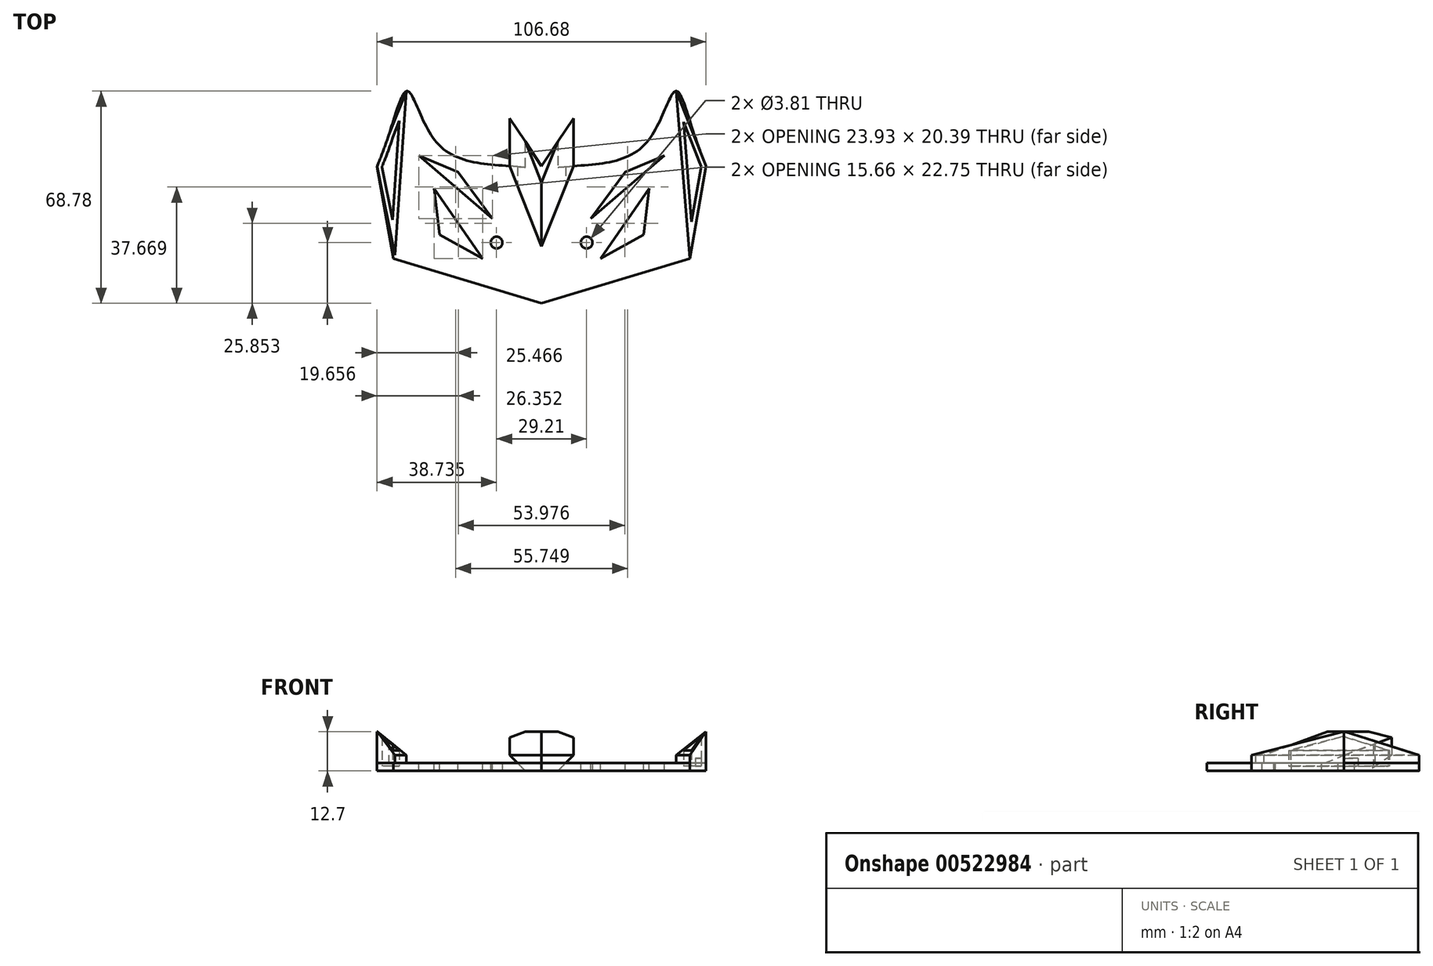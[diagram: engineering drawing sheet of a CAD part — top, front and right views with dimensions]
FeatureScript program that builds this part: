
annotation { "Feature Type Name" : "Feature", "Feature Type Description" : "" }
export const myFeature = defineFeature(function(context is Context, id is Id, definition is map)
    precondition{}
    {
        {
            var Q0;
            Q0=qCreatedBy(makeId("Top.planeOp"),FACE);
            var sketch = newSketch(context, id + "F0", { "sketchPlane" : qUnion([Q0])});
            skLineSegment(sketch, "E0", {"start": v(0, 29.97) * mm, "end": v(-10.34, 45.48) * mm});
            skLineSegment(sketch, "E1", {"start": v(-10.34, 45.48) * mm, "end": v(-10.34, 29.97) * mm});
            skPoint(sketch, "E2.1.internal.snap0", {"position": v(-10.34, 37.73) * mm});
            skFitSpline(sketch, "E2", {"points": [v(-10.34, 29.97) * mm, v(-34.11, 37.73) * mm, v(-43.42, 54.27) * mm, v(-53.34, 29.97) * mm], "startDerivative": vector(-81.15, 5.66) * mm, "endDerivative": vector(-45.03, -104.87) * mm});
            skLineSegment(sketch, "E3", {"start": v(-53.34, 29.97) * mm, "end": v(-48.07, 0) * mm});
            skLineSegment(sketch, "E4", {"start": v(-48.07, 0) * mm, "end": v(0, -14.48) * mm});
            skCircle(sketch, "E5", {"center": v(-14.6, 5.18) * mm, "radius": 1.9 * mm});
            skLineSegment(sketch, "E6", {"start": v(-43.42, 54.27) * mm, "end": v(-48.07, 0) * mm});
            skLineSegment(sketch, "E7", {"start": v(0, -14.48) * mm, "end": v(-10.34, 29.97) * mm});
            skLineSegment(sketch, "E8", {"start": v(0, -14.48) * mm, "end": v(0, 29.97) * mm});
            skLineSegment(sketch, "E9", {"start": v(-34.11, 37.73) * mm, "end": v(-26.33, -6.55) * mm});
            skLineSegment(sketch, "E10", {"start": v(-26.33, -6.55) * mm, "end": v(-19.68, 30.63) * mm});
            skLineSegment(sketch, "E11.MirrorCS", {"start": v(10.34, 45.48) * mm, "end": v(10.34, 29.97) * mm});
            skCircle(sketch, "E12.MirrorC", {"center": v(14.6, 5.18) * mm, "radius": 1.9 * mm});
            skLineSegment(sketch, "E13.MirrorCS", {"start": v(0, 29.97) * mm, "end": v(10.34, 45.48) * mm});
            skPoint(sketch, "E14.MirrorP", {"position": v(10.34, 37.73) * mm});
            skFitSpline(sketch, "E15.MirrorCS", {"points": [v(10.34, 29.97) * mm, v(34.11, 37.73) * mm, v(43.42, 54.27) * mm, v(53.34, 29.97) * mm], "startDerivative": vector(81.15, 5.66) * mm, "endDerivative": vector(45.03, -104.87) * mm});
            skLineSegment(sketch, "E16.MirrorCS", {"start": v(26.33, -6.55) * mm, "end": v(19.68, 30.63) * mm});
            skLineSegment(sketch, "E17.MirrorCS", {"start": v(53.34, 29.97) * mm, "end": v(48.07, 0) * mm});
            skLineSegment(sketch, "E18.MirrorCS", {"start": v(48.07, 0) * mm, "end": v(0, -14.48) * mm});
            skLineSegment(sketch, "E19.MirrorCS", {"start": v(43.42, 54.27) * mm, "end": v(48.07, 0) * mm});
            skLineSegment(sketch, "E20.MirrorCS", {"start": v(0, -14.48) * mm, "end": v(10.34, 29.97) * mm});
            skLineSegment(sketch, "E21.MirrorCS", {"start": v(34.11, 37.73) * mm, "end": v(26.33, -6.55) * mm});
            skLineSegment(sketch, "E22", {"start": v(-10.34, 37.73) * mm, "end": v(0, 29.97) * mm});
            skLineSegment(sketch, "E23", {"start": v(10.34, 37.73) * mm, "end": v(0, 29.97) * mm});
            skSolve(sketch);
        }
        {
            var Q0;
            Q0 = qSketchRegion(id + "F0", true);
            extrude(context, id + "F1", {"entities" : qUnion([Q0]), "depth" : 2.54 * mm, "offsetDistance" : 25.4 * mm});
        }
        {
            var Q0;
            Q0=makeQuery(id+"F1.opExtrude","CAP_FACE",FACE,{"disambiguationData":[OSD([sQuery(id+"F0.wireOp",EDGE,"E0"),sQuery(id+"F0.wireOp",EDGE,"E1"),sQuery(id+"F0.wireOp",EDGE,"E2"),sQuery(id+"F0.wireOp",EDGE,"E3"),sQuery(id+"F0.wireOp",EDGE,"E4"),sQuery(id+"F0.wireOp",EDGE,"E5"),sQuery(id+"F0.wireOp",EDGE,"E11.MirrorCS"),sQuery(id+"F0.wireOp",EDGE,"E12.MirrorC"),sQuery(id+"F0.wireOp",EDGE,"E13.MirrorCS"),sQuery(id+"F0.wireOp",EDGE,"E15.MirrorCS"),sQuery(id+"F0.wireOp",EDGE,"E17.MirrorCS"),sQuery(id+"F0.wireOp",EDGE,"E18.MirrorCS")])],"isStart":false});
            var sketch = newSketch(context, id + "F2", { "sketchPlane" : qUnion([Q0])});
            skLineSegment(sketch, "E24", {"start": v(-47.57, 1.19) * mm, "end": v(-53.34, 29.97) * mm});
            skLineSegment(sketch, "E25", {"start": v(-53.58, 30.04) * mm, "end": v(-43.9, 54.24) * mm});
            skLineSegment(sketch, "E26", {"start": v(-47.57, 1.19) * mm, "end": v(-43.9, 54.24) * mm});
            skLineSegment(sketch, "E27", {"start": v(-10.34, 29.97) * mm, "end": v(0, 3.97) * mm});
            skLineSegment(sketch, "E28", {"start": v(0, 3.97) * mm, "end": v(10.34, 29.97) * mm});
            skLineSegment(sketch, "E29", {"start": v(10.34, 29.97) * mm, "end": v(10.34, 45.48) * mm});
            skLineSegment(sketch, "E30", {"start": v(10.34, 45.48) * mm, "end": v(0, 29.97) * mm});
            skLineSegment(sketch, "E31", {"start": v(0, 29.97) * mm, "end": v(-10.34, 45.48) * mm});
            skLineSegment(sketch, "E32", {"start": v(-10.34, 45.48) * mm, "end": v(-10.34, 29.97) * mm});
            skLineSegment(sketch, "E33", {"start": v(0, 0) * mm, "end": v(0, 29.97) * mm});
            skLineSegment(sketch, "E34", {"start": v(48.07, 0) * mm, "end": v(53.34, 29.97) * mm});
            skLineSegment(sketch, "E35", {"start": v(53.34, 29.97) * mm, "end": v(43.67, 54.3) * mm});
            skLineSegment(sketch, "E36", {"start": v(43.67, 54.3) * mm, "end": v(48.07, 0) * mm});
            skSolve(sketch);
        }
        {
            var Q0;
            {var subQ0=sQuery(id+"F2.wireOp",EDGE,"E35");var subQ1=makeQuery(id+"F1.opExtrude","CAP_EDGE",EDGE,{"disambiguationData":[OSD([sQuery(id+"F0.wireOp",EDGE,"E15.MirrorCS")])],"isStart":false});var subQ3=makeQuery(id+"F2.imprint","INTERSECT",VERTEX,{"derivedFrom":[subQ1,subQ0]});Q0=makeQuery(id+"F2.imprint","IMPRINT",FACE,{"disambiguationData":[TD([[makeQuery(id+"F2.imprint","IMPRINT",EDGE,{"disambiguationData":[TD([[subQ3,1.0]])],"derivedFrom":subQ0}),1.0]])]});}
            var Q1;
            {var subQ0=sQuery(id+"F2.wireOp",EDGE,"E34");Q1=makeQuery(id+"F2.imprint","IMPRINT",FACE,{"disambiguationData":[TD([[makeQuery(id+"F2.imprint","IMPRINT",EDGE,{"derivedFrom":subQ0}),-1.0]])]});}
            var Q2;
            {var subQ0=sQuery(id+"F2.wireOp",EDGE,"E24");Q2=makeQuery(id+"F2.imprint","IMPRINT",FACE,{"disambiguationData":[TD([[makeQuery(id+"F2.imprint","IMPRINT",EDGE,{"derivedFrom":subQ0}),-1.0]])]});}
            var Q3;
            {var subQ0=sQuery(id+"F2.wireOp",EDGE,"E28");Q3=makeQuery(id+"F2.imprint","IMPRINT",FACE,{"disambiguationData":[TD([[makeQuery(id+"F2.imprint","IMPRINT",EDGE,{"derivedFrom":subQ0}),1.0]])]});}
            var Q4;
            {var subQ0=sQuery(id+"F2.wireOp",EDGE,"E27");Q4=makeQuery(id+"F2.imprint","IMPRINT",FACE,{"disambiguationData":[TD([[makeQuery(id+"F2.imprint","IMPRINT",EDGE,{"derivedFrom":subQ0}),1.0]])]});}
            extrude(context, id + "F3", {"entities" : qUnion([Q0, Q1, Q2, Q3, Q4]), "operationType" : NewBodyOperationType.ADD, "depth" : 10.16 * mm, "offsetDistance" : 25.4 * mm});
        }
        {
            var Q0;
            Q0=makeQuery(id+"F3.opExtrude","CAP_EDGE",EDGE,{"disambiguationData":[OSD([sQuery(id+"F2.wireOp",EDGE,"E26")])],"isStart":false});
            var Q1;
            Q1=makeQuery(id+"F3.opExtrude","CAP_EDGE",EDGE,{"disambiguationData":[OSD([sQuery(id+"F2.wireOp",EDGE,"E36")])],"isStart":false});
            var Q2;
            Q2=makeQuery(id+"F3.opExtrude","CAP_EDGE",EDGE,{"disambiguationData":[OSD([sQuery(id+"F2.wireOp",EDGE,"E28")])],"isStart":false});
            var Q3;
            Q3=makeQuery(id+"F3.opExtrude","CAP_EDGE",EDGE,{"disambiguationData":[OSD([sQuery(id+"F2.wireOp",EDGE,"E27")])],"isStart":false});
            chamfer(context, id + "F4", {"entities" : qUnion([Q0, Q1, Q2, Q3]), "width" : 7.62 * mm, "tangentPropagation" : true});
        }
        {
            var Q0;
            Q0=makeQuery(id+"F1.opExtrude","CAP_EDGE",EDGE,{"disambiguationData":[OSD([sQuery(id+"F0.wireOp",EDGE,"E11.MirrorCS")])],"isStart":true});
            var Q1;
            Q1=makeQuery(id+"F1.opExtrude","CAP_EDGE",EDGE,{"disambiguationData":[OSD([sQuery(id+"F0.wireOp",EDGE,"E1")])],"isStart":true});
            chamfer(context, id + "F5", {"entities" : qUnion([Q0, Q1]), "width" : 5.08 * mm, "tangentPropagation" : true});
        }
        {
            var Q0;
            Q0=makeQuery(id+"F4.opChamfer","BLEND_FACE",FACE,{"disambiguationData":[OSD([sQuery(id+"F2.wireOp",EDGE,"E36")])]});
            var Q1;
            Q1=makeQuery(id+"F4.opChamfer","BLEND_FACE",FACE,{"disambiguationData":[OSD([sQuery(id+"F2.wireOp",EDGE,"E26")])]});
            shell(context, id + "F6", {"entities" : qUnion([Q0, Q1]), "thickness" : 1.52 * mm});
        }
        {
            var Q0;
            {var subQ0=sQuery(id+"F0.wireOp",EDGE,"E17.MirrorCS");var subQ1=sQuery(id+"F0.wireOp",EDGE,"E15.MirrorCS");var subQ2=sQuery(id+"F0.wireOp",EDGE,"E12.MirrorC");var subQ3=sQuery(id+"F0.wireOp",EDGE,"E11.MirrorCS");var subQ4=sQuery(id+"F0.wireOp",EDGE,"E5");var subQ5=sQuery(id+"F0.wireOp",EDGE,"E4");var subQ6=sQuery(id+"F0.wireOp",EDGE,"E18.MirrorCS");var subQ7=sQuery(id+"F0.wireOp",EDGE,"E3");var subQ8=sQuery(id+"F0.wireOp",EDGE,"E2");var subQ9=sQuery(id+"F0.wireOp",EDGE,"E1");var subQ10=makeQuery(id+"F1.opExtrude","CAP_FACE",FACE,{"disambiguationData":[OSD([sQuery(id+"F0.wireOp",EDGE,"E0"),subQ9,subQ8,subQ7,subQ5,subQ4,subQ3,subQ2,sQuery(id+"F0.wireOp",EDGE,"E13.MirrorCS"),subQ1,subQ0,subQ6])],"isStart":false});Q0=makeQuery(id+"F3.boolean.opBoolean","SPLIT",FACE,{"disambiguationData":[TD([subQ10,makeQuery(id+"F1.opExtrude","SWEPT_FACE",FACE,{"disambiguationData":[OSD([subQ9])]}),makeQuery(id+"F1.opExtrude","SWEPT_FACE",FACE,{"disambiguationData":[OSD([subQ8])]}),makeQuery(id+"F1.opExtrude","SWEPT_FACE",FACE,{"disambiguationData":[OSD([subQ7])]}),makeQuery(id+"F1.opExtrude","SWEPT_FACE",FACE,{"disambiguationData":[OSD([subQ5])]}),makeQuery(id+"F1.opExtrude","SWEPT_FACE",FACE,{"disambiguationData":[OSD([subQ4])]}),makeQuery(id+"F1.opExtrude","SWEPT_FACE",FACE,{"disambiguationData":[OSD([subQ3])]}),makeQuery(id+"F1.opExtrude","SWEPT_FACE",FACE,{"disambiguationData":[OSD([subQ2])]}),makeQuery(id+"F1.opExtrude","SWEPT_FACE",FACE,{"disambiguationData":[OSD([subQ1])]}),makeQuery(id+"F1.opExtrude","SWEPT_FACE",FACE,{"disambiguationData":[OSD([subQ0])]}),makeQuery(id+"F1.opExtrude","SWEPT_FACE",FACE,{"disambiguationData":[OSD([subQ6])]}),makeQuery(id+"F3.opExtrude","SWEPT_FACE",FACE,{"disambiguationData":[OSD([sQuery(id+"F2.wireOp",EDGE,"E24")])]}),makeQuery(id+"F3.opExtrude","SWEPT_FACE",FACE,{"disambiguationData":[OSD([sQuery(id+"F2.wireOp",EDGE,"E25")])]}),makeQuery(id+"F3.opExtrude","SWEPT_FACE",FACE,{"disambiguationData":[OSD([sQuery(id+"F2.wireOp",EDGE,"E26")])]}),makeQuery(id+"F3.opExtrude","SWEPT_FACE",FACE,{"disambiguationData":[OSD([sQuery(id+"F2.wireOp",EDGE,"E27")])]}),makeQuery(id+"F3.opExtrude","SWEPT_FACE",FACE,{"disambiguationData":[OSD([sQuery(id+"F2.wireOp",EDGE,"E28")])]}),makeQuery(id+"F3.opExtrude","SWEPT_FACE",FACE,{"disambiguationData":[OSD([sQuery(id+"F2.wireOp",EDGE,"E29")])]}),makeQuery(id+"F3.opExtrude","SWEPT_FACE",FACE,{"disambiguationData":[OSD([sQuery(id+"F2.wireOp",EDGE,"E32")])]}),makeQuery(id+"F3.opExtrude","SWEPT_FACE",FACE,{"disambiguationData":[OSD([sQuery(id+"F2.wireOp",EDGE,"E34")])]}),makeQuery(id+"F3.opExtrude","SWEPT_FACE",FACE,{"disambiguationData":[OSD([sQuery(id+"F2.wireOp",EDGE,"E35")])]}),makeQuery(id+"F3.opExtrude","SWEPT_FACE",FACE,{"disambiguationData":[OSD([sQuery(id+"F2.wireOp",EDGE,"E36")])]}),makeQuery(id+"F3.opExtrude","SWEPT_FACE",FACE,{"disambiguationData":[OSD([subQ8])]})])],"derivedFrom":subQ10});}
            var sketch = newSketch(context, id + "F7", { "sketchPlane" : qUnion([Q0])});
            skLineSegment(sketch, "E37", {"start": v(-34.82, 22.75) * mm, "end": v(-19.16, 0) * mm});
            skLineSegment(sketch, "E38", {"start": v(-19.16, 0) * mm, "end": v(-33.05, 7.68) * mm});
            skLineSegment(sketch, "E39", {"start": v(-33.05, 7.68) * mm, "end": v(-34.82, 22.75) * mm});
            skLineSegment(sketch, "E40", {"start": v(-27.14, 28.07) * mm, "end": v(-15.9, 13) * mm});
            skLineSegment(sketch, "E41", {"start": v(-15.9, 13) * mm, "end": v(-39.84, 33.38) * mm});
            skLineSegment(sketch, "E42", {"start": v(-39.84, 33.38) * mm, "end": v(-27.14, 28.07) * mm});
            skLineSegment(sketch, "E43.MirrorCS", {"start": v(27.14, 28.07) * mm, "end": v(15.9, 13) * mm});
            skLineSegment(sketch, "E44.MirrorCS", {"start": v(39.84, 33.38) * mm, "end": v(27.14, 28.07) * mm});
            skLineSegment(sketch, "E45.MirrorCS", {"start": v(15.9, 13) * mm, "end": v(39.84, 33.38) * mm});
            skLineSegment(sketch, "E46.MirrorCS", {"start": v(34.82, 22.75) * mm, "end": v(19.16, 0) * mm});
            skLineSegment(sketch, "E47.MirrorCS", {"start": v(33.05, 7.68) * mm, "end": v(34.82, 22.75) * mm});
            skLineSegment(sketch, "E48.MirrorCS", {"start": v(19.16, 0) * mm, "end": v(33.05, 7.68) * mm});
            skSolve(sketch);
        }
        {
            var Q0;
            Q0 = qSketchRegion(id + "F7", true);
            extrude(context, id + "F8", {"entities" : qUnion([Q0]), "operationType" : NewBodyOperationType.REMOVE, "endBound" : BoundingType.THROUGH_ALL, "oppositeDirection" : true, "depth" : 25.4 * mm, "offsetDistance" : 25.4 * mm});
        }
    });
